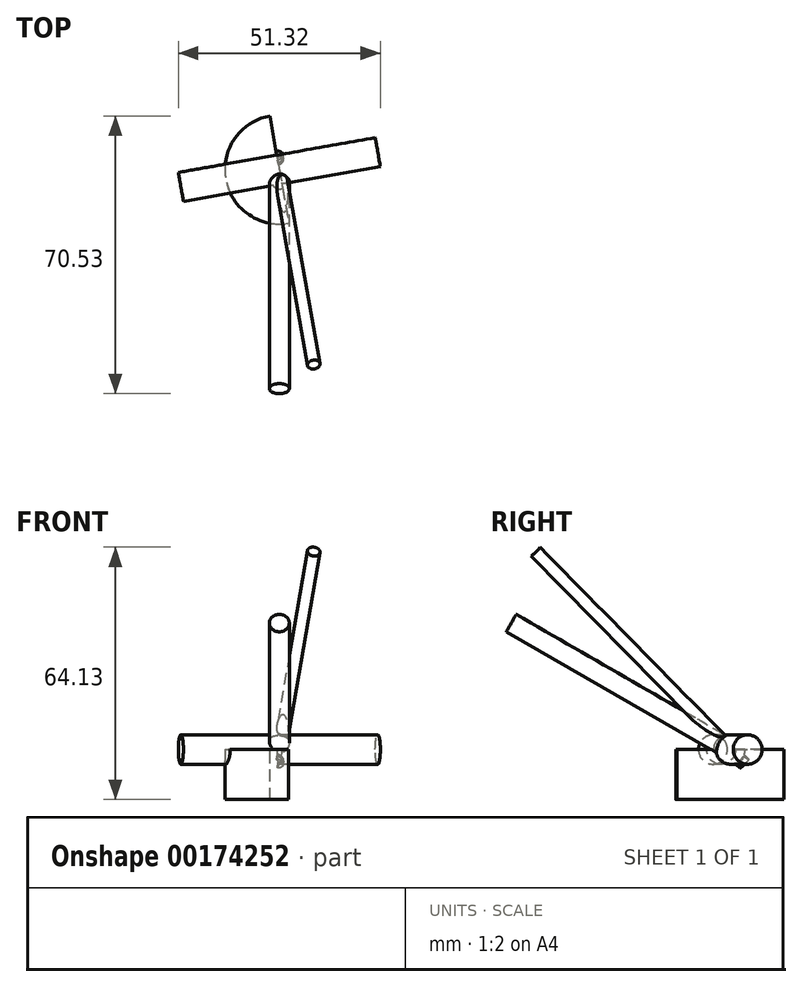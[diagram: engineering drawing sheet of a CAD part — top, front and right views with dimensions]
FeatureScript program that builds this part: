
annotation { "Feature Type Name" : "Feature", "Feature Type Description" : "" }
export const myFeature = defineFeature(function(context is Context, id is Id, definition is map)
    precondition{}
    {
        {
            var Q0;
            Q0=qCreatedBy(makeId("Right.planeOp"),FACE);
            var sketch = newSketch(context, id + "F0", { "sketchPlane" : qUnion([Q0])});
            skLineSegment(sketch, "E0", {"start": v(0, 0) * mm, "end": v(-67.2, 38.8) * mm, "construction": true});
            skLineSegment(sketch, "E1", {"start": v(-55.65, 32.13) * mm, "end": v(-54.38, 34.33) * mm});
            skLineSegment(sketch, "E2", {"start": v(-54.38, 34.33) * mm, "end": v(0.61, 2.58) * mm});
            skLineSegment(sketch, "E3", {"start": v(0.61, 2.58) * mm, "end": v(0, 0) * mm});
            skLineSegment(sketch, "E4", {"start": v(-55.65, 32.13) * mm, "end": v(0, 0) * mm});
            skSolve(sketch);
        }
        {
            var Q0;
            Q0=qCreatedBy(makeId("Right.planeOp"),FACE);
            var sketch = newSketch(context, id + "F1", { "sketchPlane" : qUnion([Q0])});
            skLineSegment(sketch, "E5", {"start": v(0, 0) * mm, "end": v(-79, 0) * mm, "construction": true});
            skSolve(sketch);
        }
        {
            var Q0;
            Q0=sQuery(id+"F1.wireOp",EDGE,"E5");
            cPlane(context, id + "F2", {"entities" : qUnion([Q0]), "cplaneType" : CPlaneType.LINE_ANGLE, "offset" : 25.4 * mm, "angle" : 0 * degree, "width" : 152.4 * mm, "height" : 152.4 * mm});
        }
        {
            var Q0;
            Q0 = qSketchRegion(id + "F0", true);
            var Q1;
            Q1=sQuery(id+"F0.wireOp",EDGE,"E0");
            revolve(context, id + "F3", {"entities" : qUnion([Q0]), "axis" : qUnion([Q1]), "revolveType" : RevolveType.FULL});
        }
        {
            var Q0;
            Q0=qCreatedBy(id+"F2.planeOp",FACE);
            var sketch = newSketch(context, id + "F4", { "sketchPlane" : qUnion([Q0])});
            skLineSegment(sketch, "E6", {"start": v(0, 0) * mm, "end": v(-28.5, 0) * mm, "construction": true});
            skArc(sketch, "E7", {"start": v(2.4, 13.61) * mm, "mid": v(-13.61, 2.4) * mm, "end": v(-2.4, -13.61) * mm});
            skLineSegment(sketch, "E8", {"start": v(-2.4, -13.61) * mm, "end": v(0, 0) * mm});
            skLineSegment(sketch, "E9", {"start": v(0, 0) * mm, "end": v(2.4, 13.61) * mm});
            skSolve(sketch);
        }
        {
            var Q0;
            Q0 = qSketchRegion(id + "F4", true);
            extrude(context, id + "F5", {"entities" : qUnion([Q0]), "depth" : 12.7 * mm});
        }
        {
            var Q0;
            Q0=makeQuery(id+"F5.opExtrude","SWEPT_FACE",FACE,{"disambiguationData":[OSD([sQuery(id+"F4.wireOp",EDGE,"E8"),sQuery(id+"F4.wireOp",EDGE,"E9")])]});
            var sketch = newSketch(context, id + "F6", { "sketchPlane" : qUnion([Q0])});
            skLineSegment(sketch, "E10", {"start": v(0, 0) * mm, "end": v(-61.97, 61.97) * mm, "construction": true});
            skLineSegment(sketch, "E11", {"start": v(0, 0) * mm, "end": v(-50.3, 50.3) * mm});
            skLineSegment(sketch, "E12", {"start": v(-51.43, 49.17) * mm, "end": v(-50.3, 50.3) * mm});
            skLineSegment(sketch, "E13", {"start": v(-51.43, 49.17) * mm, "end": v(2.45, -4.72) * mm});
            skLineSegment(sketch, "E14", {"start": v(2.45, -4.72) * mm, "end": v(0, 0) * mm});
            skLineSegment(sketch, "E15", {"start": v(13.56, 0) * mm, "end": v(61.9, 0) * mm, "construction": true});
            skSolve(sketch);
        }
        {
            var Q0;
            Q0 = qSketchRegion(id + "F6", true);
            var Q1;
            Q1=sQuery(id+"F6.wireOp",EDGE,"E10");
            revolve(context, id + "F7", {"entities" : qUnion([Q0]), "axis" : qUnion([Q1]), "revolveType" : RevolveType.FULL});
        }
        {
            var Q0;
            Q0=makeQuery(id+"F5.opExtrude","SWEPT_FACE",FACE,{"disambiguationData":[OSD([sQuery(id+"F4.wireOp",EDGE,"E8"),sQuery(id+"F4.wireOp",EDGE,"E9")])]});
            var sketch = newSketch(context, id + "F8", { "sketchPlane" : qUnion([Q0])});
            skCircle(sketch, "E16", {"center": v(0, 0) * mm, "radius": 3.73 * mm});
            skSolve(sketch);
        }
        {
            var Q0;
            Q0 = qSketchRegion(id + "F8", true);
            extrude(context, id + "F9", {"entities" : qUnion([Q0]), "operationType" : NewBodyOperationType.ADD, "depth" : 25.4 * mm, "hasSecondDirection" : true, "secondDirectionOppositeDirection" : true, "secondDirectionDepth" : 25.4 * mm});
        }
    });
